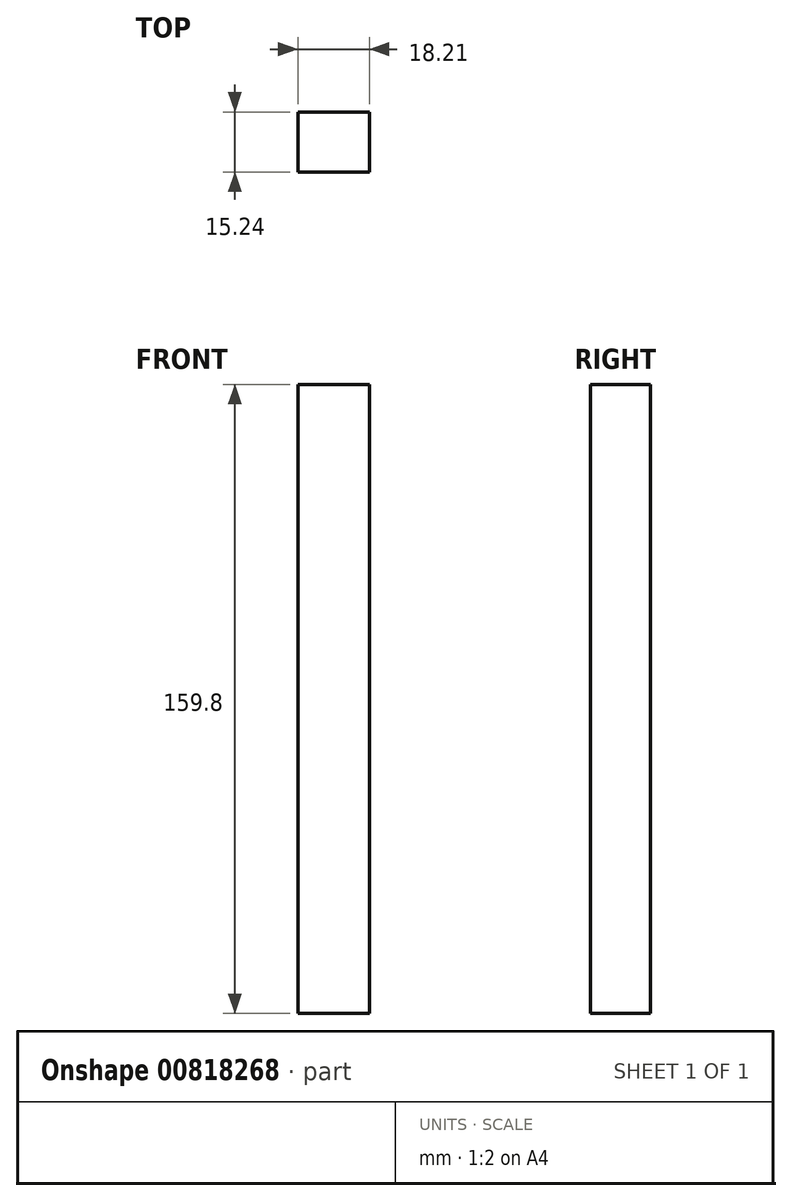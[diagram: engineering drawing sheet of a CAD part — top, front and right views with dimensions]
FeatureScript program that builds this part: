
annotation { "Feature Type Name" : "Feature", "Feature Type Description" : "" }
export const myFeature = defineFeature(function(context is Context, id is Id, definition is map)
    precondition{}
    {
        {
            var Q0;
            Q0=qCreatedBy(makeId("Front.planeOp"),FACE);
            var sketch = newSketch(context, id + "F0", { "sketchPlane" : qUnion([Q0])});
            skLineSegment(sketch, "E0.bottom", {"start": v(-35.66, -79.9) * mm, "end": v(-53.87, -79.9) * mm});
            skLineSegment(sketch, "E0.top", {"start": v(-35.66, 79.9) * mm, "end": v(-53.87, 79.9) * mm});
            skLineSegment(sketch, "E0.left", {"start": v(-35.66, -79.9) * mm, "end": v(-35.66, 79.9) * mm});
            skLineSegment(sketch, "E0.right", {"start": v(-53.87, -79.9) * mm, "end": v(-53.87, 79.9) * mm});
            skPoint(sketch, "E0.middle", {"position": v(-44.77, 0) * mm});
            skSolve(sketch);
        }
        {
            var Q0;
            Q0 = qSketchRegion(id + "F0", true);
            extrude(context, id + "F1", {"entities" : qUnion([Q0]), "oppositeDirection" : true, "depth" : 15.24 * mm, "offsetDistance" : 25.4 * mm});
        }
    });
